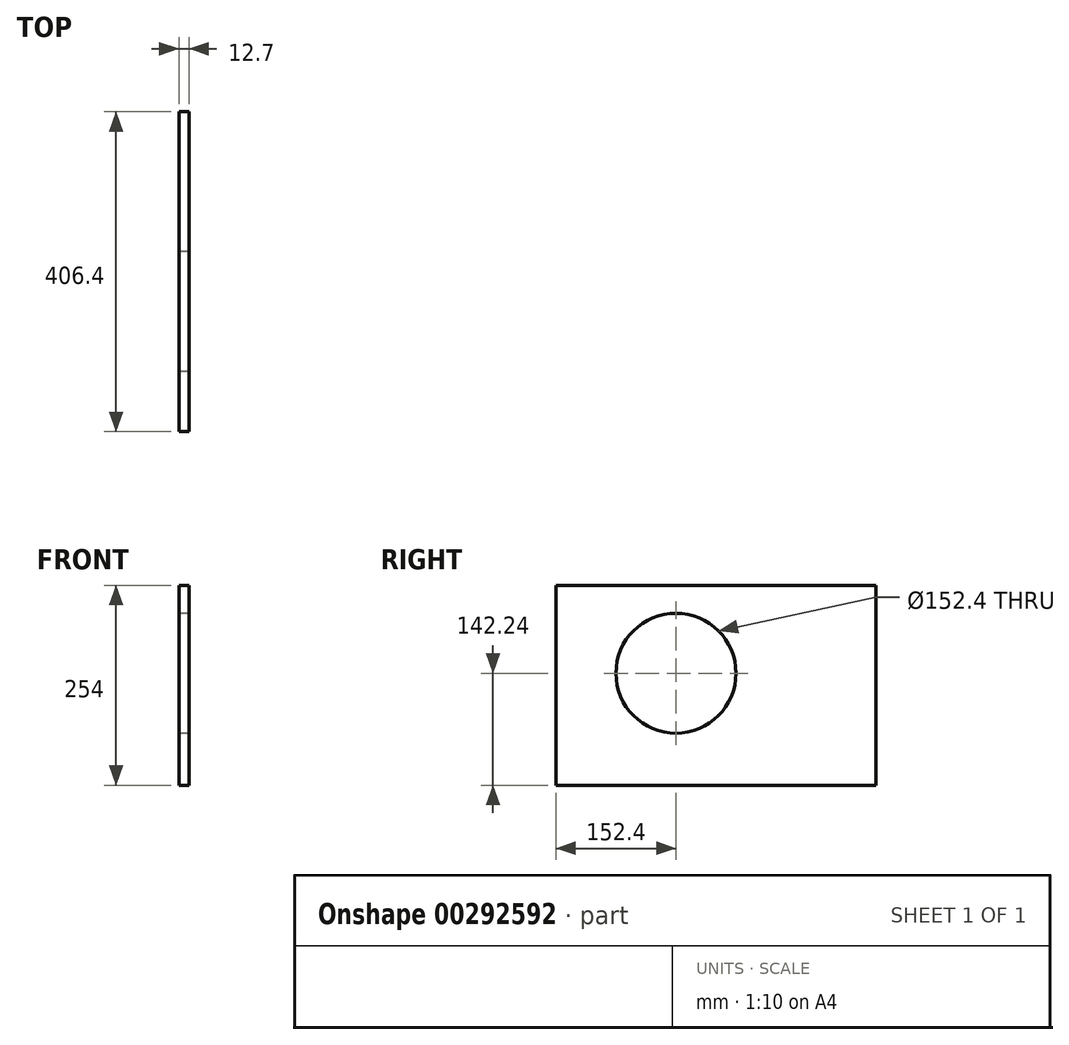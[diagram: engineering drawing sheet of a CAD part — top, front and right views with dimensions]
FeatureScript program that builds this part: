
annotation { "Feature Type Name" : "Feature", "Feature Type Description" : "" }
export const myFeature = defineFeature(function(context is Context, id is Id, definition is map)
    precondition{}
    {
        {
            var Q0;
            Q0=qCreatedBy(makeId("Right.planeOp"),FACE);
            var sketch = newSketch(context, id + "F0", { "sketchPlane" : qUnion([Q0])});
            skLineSegment(sketch, "E0.bottom", {"start": v(0, 0) * mm, "end": v(406.4, 0) * mm});
            skLineSegment(sketch, "E0.top", {"start": v(0, 254) * mm, "end": v(406.4, 254) * mm});
            skLineSegment(sketch, "E0.left", {"start": v(0, 0) * mm, "end": v(0, 254) * mm});
            skLineSegment(sketch, "E0.right", {"start": v(406.4, 0) * mm, "end": v(406.4, 254) * mm});
            skCircle(sketch, "E1", {"center": v(152.4, 142.24) * mm, "radius": 76.2 * mm});
            skSolve(sketch);
        }
        {
            var Q0;
            Q0=makeQuery(id+"F0.imprint","IMPRINT",FACE,{"disambiguationData":[TD([[makeQuery(id+"F0.imprint","IMPRINT",EDGE,{"derivedFrom":sQuery(id+"F0.wireOp",EDGE,"E0.bottom")}),1.0]])]});
            extrude(context, id + "F1", {"entities" : qUnion([Q0]), "depth" : 12.7 * mm});
        }
    });
